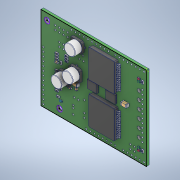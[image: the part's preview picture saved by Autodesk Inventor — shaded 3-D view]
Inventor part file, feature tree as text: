
AUTODESK INVENTOR PART (.ipt)
format: ipt  version: 2020 (Build 240168000, 168)  size: 1,911,808 bytes
history: native  units: in
note: dims shown in document units (in); Inventor stores cm internally (conversion verified against a paired STEP export)
features: sketch x1, boolean_combine x1
ambient origin geometry x8: Origin, YZ Plane, XZ Plane, XY Plane, X Axis, Y Axis, Z Axis, Center Point
bodies: Solid1 (feature_tree)
feature tree (2):
  sketch  "Sketch1"
  boolean_combine  "Combine1"
